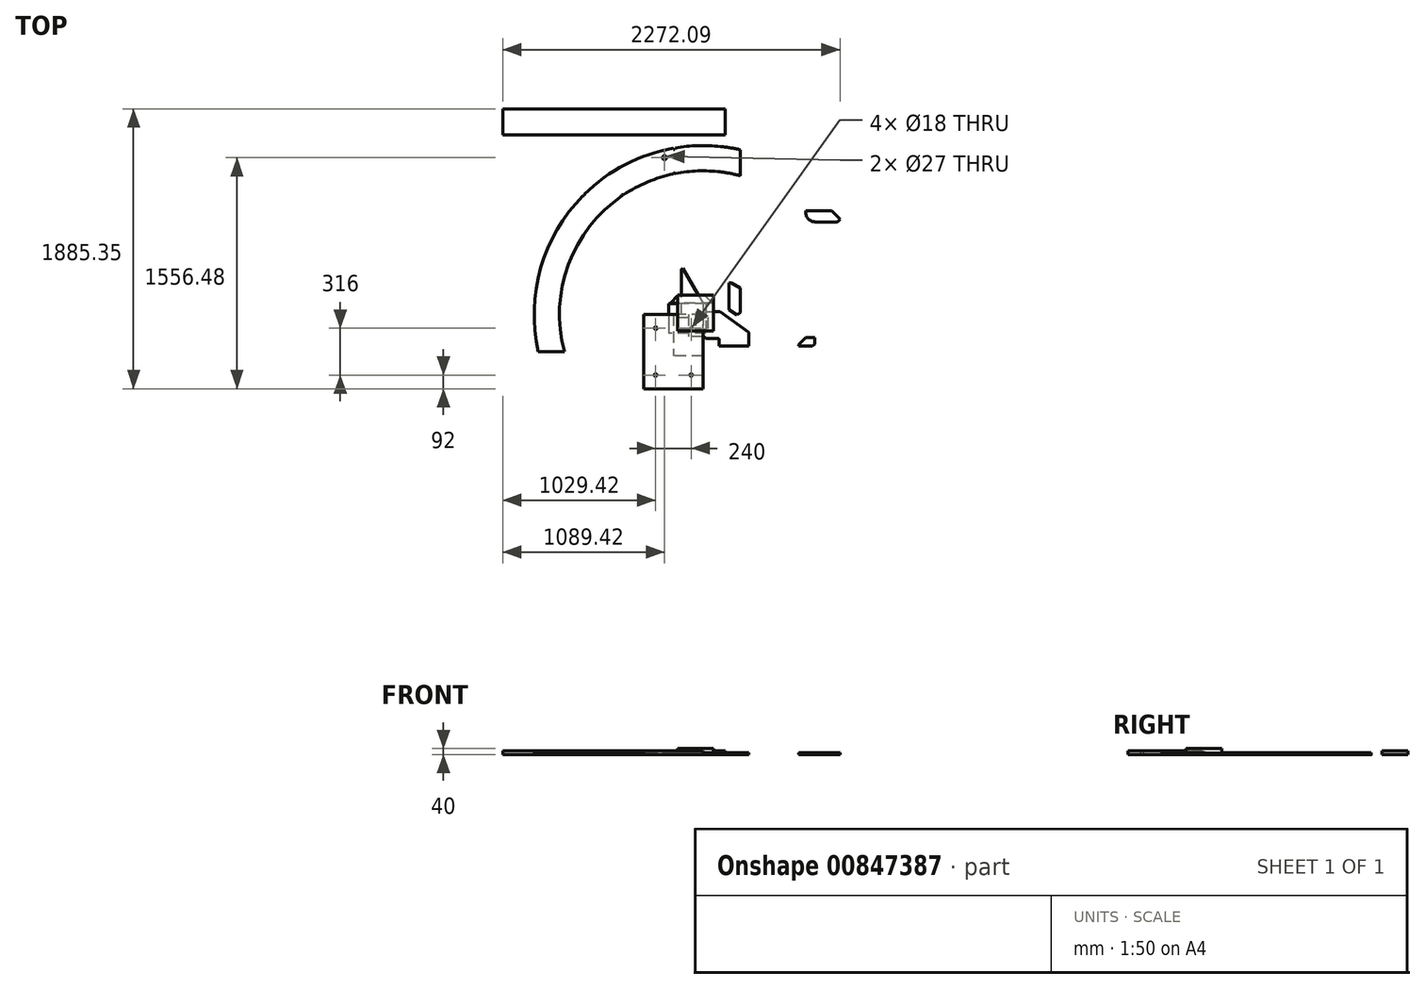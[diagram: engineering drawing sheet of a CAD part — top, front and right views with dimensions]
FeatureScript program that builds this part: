
annotation { "Feature Type Name" : "Feature", "Feature Type Description" : "" }
export const myFeature = defineFeature(function(context is Context, id is Id, definition is map)
    precondition{}
    {
        {
            var Q0;
            Q0=qCreatedBy(makeId("Top.planeOp"),FACE);
            var sketch = newSketch(context, id + "F0", { "sketchPlane" : qUnion([Q0])});
            skArc(sketch, "E0", {"start": v(250.54, 935.02) * mm, "mid": v(186.68, 949.83) * mm, "end": v(121.98, 960.28) * mm});
            skLineSegment(sketch, "E1", {"start": v(250.54, 935.02) * mm, "end": v(250.54, 1110.08) * mm});
            skLineSegment(sketch, "E2", {"start": v(-935.02, -250.54) * mm, "end": v(-1110.08, -250.54) * mm});
            skCircle(sketch, "E3", {"center": v(-260, 1056.48) * mm, "radius": 13.5 * mm});
            skLineSegment(sketch, "E4", {"start": v(-200, 1120.29) * mm, "end": v(-200, 1111.78) * mm});
            skLineSegment(sketch, "E5", {"start": v(116, 1132.07) * mm, "end": v(116, 1126.07) * mm});
            skLineSegment(sketch, "E6", {"start": v(-809.35, 800) * mm, "end": v(-799.3, 800) * mm});
            skLineSegment(sketch, "E7", {"start": v(-799.3, 800) * mm, "end": v(-799.3, 810.04) * mm});
            skLineSegment(sketch, "E8", {"start": v(-200, 1111.78) * mm, "end": v(-191.98, 1111.78) * mm});
            skLineSegment(sketch, "E9", {"start": v(-191.98, 1111.78) * mm, "end": v(-187.26, 1122.49) * mm});
            skLineSegment(sketch, "E10", {"start": v(-200, 954.9) * mm, "end": v(-186.65, 949.83) * mm});
            skLineSegment(sketch, "E11", {"start": v(116, 1126.07) * mm, "end": v(121.39, 1131.5) * mm});
            skLineSegment(sketch, "E12", {"start": v(116, 968.66) * mm, "end": v(121.98, 960.28) * mm});
            skArc(sketch, "E13.trimOffspring", {"start": v(250.54, 1110.08) * mm, "mid": v(186.27, 1122.65) * mm, "end": v(121.39, 1131.5) * mm});
            skPoint(sketch, "E14.start.orphan", {"position": v(0, 1199.9) * mm});
            skLineSegment(sketch, "E15.trimOffspring", {"start": v(-200, 954.9) * mm, "end": v(-200, 947.11) * mm});
            skLineSegment(sketch, "E16.trimOffspring", {"start": v(116, 968.66) * mm, "end": v(116, 961.02) * mm});
            skLineSegment(sketch, "E17.trimOffspring", {"start": v(-550.8, 800) * mm, "end": v(-545, 800) * mm});
            skArc(sketch, "E18.trimOffspring", {"start": v(-809.35, 800) * mm, "mid": v(-1094.06, 313.19) * mm, "end": v(-1110.08, -250.54) * mm});
            skLineSegment(sketch, "E19", {"start": v(-550.8, 800) * mm, "end": v(-550.8, 806.6) * mm});
            skLineSegment(sketch, "E20", {"start": v(-550.8, 806.6) * mm, "end": v(-535.17, 806.6) * mm});
            skArc(sketch, "E21.trimOffspring", {"start": v(-545, 800) * mm, "mid": v(-907.48, 336.9) * mm, "end": v(-935.02, -250.54) * mm});
            skArc(sketch, "E22.trimOffspring", {"start": v(-200, 1120.29) * mm, "mid": v(-523.18, 1010.6) * mm, "end": v(-799.3, 810.04) * mm});
            skArc(sketch, "E23.trimOffspring", {"start": v(-200, 947.11) * mm, "mid": v(-374.24, 892.73) * mm, "end": v(-535.17, 806.6) * mm});
            skArc(sketch, "E24.trimOffspring", {"start": v(116, 961.02) * mm, "mid": v(-35.76, 967.34) * mm, "end": v(-186.65, 949.83) * mm});
            skArc(sketch, "E25.trimOffspring", {"start": v(116, 1132.07) * mm, "mid": v(-35.95, 1137.43) * mm, "end": v(-187.26, 1122.49) * mm});
            skLineSegment(sketch, "E26.bottom", {"start": v(691.59, 699.24) * mm, "end": v(866.59, 699.24) * mm});
            skLineSegment(sketch, "E26.top", {"start": v(756.59, 624.24) * mm, "end": v(866.59, 624.24) * mm});
            skLineSegment(sketch, "E26.left", {"start": v(691.59, 699.24) * mm, "end": v(691.59, 689.24) * mm});
            skLineSegment(sketch, "E26.right", {"start": v(866.59, 699.24) * mm, "end": v(866.59, 624.24) * mm});
            skLineSegment(sketch, "E27", {"start": v(866.59, 699.24) * mm, "end": v(922.67, 643.16) * mm});
            skLineSegment(sketch, "E28", {"start": v(903.76, 624.24) * mm, "end": v(866.59, 624.24) * mm});
            skLineSegment(sketch, "E29", {"start": v(922.67, 643.16) * mm, "end": v(903.76, 624.24) * mm});
            skPoint(sketch, "E30.visualSharp", {"position": v(691.59, 624.24) * mm});
            skArc(sketch, "E30.filletArc", {"start": v(691.59, 689.24) * mm, "mid": v(710.63, 643.28) * mm, "end": v(756.59, 624.24) * mm});
            skPoint(sketch, "E31.orphan", {"position": v(941.59, 624.24) * mm});
            skSolve(sketch);
        }
        {
            var Q0;
            Q0 = qSketchRegion(id + "F0", true);
            extrude(context, id + "F1", {"entities" : qUnion([Q0]), "depth" : 12 * mm, "offsetDistance" : 25 * mm});
        }
        {
            var Q0;
            Q0=qCreatedBy(makeId("Top.planeOp"),FACE);
            var sketch = newSketch(context, id + "F2", { "sketchPlane" : qUnion([Q0])});
            skLineSegment(sketch, "E32.bottom", {"start": v(175.87, 213.2) * mm, "end": v(190.87, 213.2) * mm});
            skLineSegment(sketch, "E32.left", {"start": v(175.87, 213.2) * mm, "end": v(175.87, 33.2) * mm});
            skLineSegment(sketch, "E32.right", {"start": v(250.87, 178.2) * mm, "end": v(250.87, 12.2) * mm});
            skLineSegment(sketch, "E33", {"start": v(190.87, 213.2) * mm, "end": v(250.87, 178.2) * mm});
            skLineSegment(sketch, "E34", {"start": v(175.87, 33.2) * mm, "end": v(227.87, -3.8) * mm});
            skLineSegment(sketch, "E35", {"start": v(227.87, -3.8) * mm, "end": v(250.87, 12.2) * mm});
            skSolve(sketch);
        }
        {
            var Q0;
            Q0 = qSketchRegion(id + "F2", true);
            extrude(context, id + "F3", {"entities" : qUnion([Q0]), "depth" : 10 * mm, "offsetDistance" : 25 * mm});
        }
        {
            var Q0;
            Q0=qCreatedBy(makeId("Top.planeOp"),FACE);
            var sketch = newSketch(context, id + "F4", { "sketchPlane" : qUnion([Q0])});
            skLineSegment(sketch, "E36", {"start": v(-166.74, 130.62) * mm, "end": v(9.26, 130.62) * mm});
            skLineSegment(sketch, "E37", {"start": v(9.26, 130.62) * mm, "end": v(62.3, 77.58) * mm});
            skLineSegment(sketch, "E38", {"start": v(62.3, 77.58) * mm, "end": v(-219.77, 77.58) * mm});
            skLineSegment(sketch, "E39", {"start": v(-219.77, 77.58) * mm, "end": v(-166.74, 130.62) * mm});
            skPoint(sketch, "E40.end.orphan", {"position": v(-166.74, 184.48) * mm});
            skSolve(sketch);
        }
        {
            var Q0;
            Q0 = qSketchRegion(id + "F4", true);
            extrude(context, id + "F5", {"entities" : qUnion([Q0]), "depth" : 10 * mm, "offsetDistance" : 25 * mm});
        }
        {
            var Q0;
            Q0 = qSketchRegion(id + "F0", true);
            extrude(context, id + "F6", {"entities" : qUnion([Q0]), "depth" : 10 * mm, "offsetDistance" : 25 * mm});
        }
        {
            var Q0;
            Q0=qCreatedBy(makeId("Top.planeOp"),FACE);
            var sketch = newSketch(context, id + "F7", { "sketchPlane" : qUnion([Q0])});
            skLineSegment(sketch, "E41.bottom", {"start": v(-1349.42, 1385.35) * mm, "end": v(150.58, 1385.35) * mm});
            skLineSegment(sketch, "E41.top", {"start": v(-1349.42, 1209.35) * mm, "end": v(150.58, 1209.35) * mm});
            skLineSegment(sketch, "E41.left", {"start": v(-1349.42, 1385.35) * mm, "end": v(-1349.42, 1209.35) * mm});
            skLineSegment(sketch, "E41.right", {"start": v(150.58, 1385.35) * mm, "end": v(150.58, 1209.35) * mm});
            skSolve(sketch);
        }
        {
            var Q0;
            Q0 = qSketchRegion(id + "F7", true);
            extrude(context, id + "F8", {"entities" : qUnion([Q0]), "depth" : 12 * mm, "offsetDistance" : 25 * mm});
        }
        {
            var Q0;
            Q0 = qSketchRegion(id + "F7", true);
            extrude(context, id + "F9", {"entities" : qUnion([Q0]), "operationType" : NewBodyOperationType.ADD, "depth" : 25 * mm, "offsetDistance" : 25 * mm});
        }
        {
            var Q0;
            Q0=qCreatedBy(makeId("Top.planeOp"),FACE);
            var sketch = newSketch(context, id + "F10", { "sketchPlane" : qUnion([Q0])});
            skLineSegment(sketch, "E42", {"start": v(750.99, -155) * mm, "end": v(750.99, -198) * mm});
            skLineSegment(sketch, "E43", {"start": v(750.99, -198) * mm, "end": v(735.99, -213) * mm});
            skLineSegment(sketch, "E44", {"start": v(735.99, -213) * mm, "end": v(642.99, -213) * mm});
            skLineSegment(sketch, "E45", {"start": v(642.99, -213) * mm, "end": v(642.99, -203) * mm});
            skLineSegment(sketch, "E46", {"start": v(642.99, -203) * mm, "end": v(692.99, -155) * mm});
            skLineSegment(sketch, "E47", {"start": v(692.99, -155) * mm, "end": v(750.99, -155) * mm});
            skSolve(sketch);
        }
        {
            var Q0;
            Q0 = qSketchRegion(id + "F10", true);
            extrude(context, id + "F11", {"entities" : qUnion([Q0]), "depth" : 12 * mm, "offsetDistance" : 25 * mm});
        }
        {
            var Q0;
            Q0=qCreatedBy(makeId("Top.planeOp"),FACE);
            var sketch = newSketch(context, id + "F12", { "sketchPlane" : qUnion([Q0])});
            skLineSegment(sketch, "E48.bottom", {"start": v(0, 0) * mm, "end": v(-400, 0) * mm});
            skLineSegment(sketch, "E48.top", {"start": v(0, -500) * mm, "end": v(-400, -500) * mm});
            skLineSegment(sketch, "E48.left", {"start": v(0, 0) * mm, "end": v(0, -500) * mm});
            skLineSegment(sketch, "E48.right", {"start": v(-400, 0) * mm, "end": v(-400, -500) * mm});
            skCircle(sketch, "E49", {"center": v(-320, -92) * mm, "radius": 9 * mm});
            skCircle(sketch, "E50", {"center": v(-80, -92) * mm, "radius": 9 * mm});
            skCircle(sketch, "E51", {"center": v(-80, -408) * mm, "radius": 9 * mm});
            skCircle(sketch, "E52", {"center": v(-320, -408) * mm, "radius": 9 * mm});
            skSolve(sketch);
        }
        {
            var Q0;
            Q0 = qSketchRegion(id + "F12", true);
            extrude(context, id + "F13", {"entities" : qUnion([Q0]), "depth" : 16 * mm, "offsetDistance" : 25 * mm});
        }
        {
            var Q0;
            Q0 = qSketchRegion(id + "F12", true);
            extrude(context, id + "F14", {"entities" : qUnion([Q0]), "operationType" : NewBodyOperationType.ADD, "depth" : 25 * mm, "offsetDistance" : 25 * mm});
        }
        {
            var Q0;
            Q0=qCreatedBy(makeId("Top.planeOp"),FACE);
            var sketch = newSketch(context, id + "F15", { "sketchPlane" : qUnion([Q0])});
            skLineSegment(sketch, "E53", {"start": v(0, 0) * mm, "end": v(20, 20) * mm});
            skLineSegment(sketch, "E54", {"start": v(20, 20) * mm, "end": v(113, 20) * mm});
            skLineSegment(sketch, "E55", {"start": v(113, 20) * mm, "end": v(308, -121) * mm});
            skLineSegment(sketch, "E56", {"start": v(308, -121) * mm, "end": v(308, -211) * mm});
            skLineSegment(sketch, "E57", {"start": v(308, -211) * mm, "end": v(108, -211) * mm});
            skLineSegment(sketch, "E58", {"start": v(108, -211) * mm, "end": v(108, -171) * mm});
            skLineSegment(sketch, "E59", {"start": v(98, -161) * mm, "end": v(20, -161) * mm});
            skLineSegment(sketch, "E60", {"start": v(20, -161) * mm, "end": v(0, -141) * mm});
            skLineSegment(sketch, "E61", {"start": v(0, -141) * mm, "end": v(0, 0) * mm});
            skPoint(sketch, "E62.visualSharp", {"position": v(108, -161) * mm});
            skArc(sketch, "E62.filletArc", {"start": v(108, -171) * mm, "mid": v(105.07, -163.93) * mm, "end": v(98, -161) * mm});
            skSolve(sketch);
        }
        {
            var Q0;
            Q0 = qSketchRegion(id + "F15", true);
            extrude(context, id + "F16", {"entities" : qUnion([Q0]), "depth" : 12 * mm, "offsetDistance" : 25 * mm});
        }
        {
            var Q0;
            Q0=qCreatedBy(makeId("Top.planeOp"),FACE);
            var sketch = newSketch(context, id + "F17", { "sketchPlane" : qUnion([Q0])});
            skLineSegment(sketch, "E63.bottom", {"start": v(0, 0) * mm, "end": v(-100, 0) * mm});
            skLineSegment(sketch, "E63.top", {"start": v(0, -150) * mm, "end": v(-100, -150) * mm});
            skLineSegment(sketch, "E63.left", {"start": v(0, 0) * mm, "end": v(0, -150) * mm});
            skLineSegment(sketch, "E63.right", {"start": v(-100, 0) * mm, "end": v(-100, -150) * mm});
            skSolve(sketch);
        }
        {
            var Q0;
            Q0 = qSketchRegion(id + "F17", true);
            extrude(context, id + "F18", {"entities" : qUnion([Q0]), "depth" : 8 * mm, "offsetDistance" : 25 * mm});
        }
        {
            var Q0;
            Q0=qCreatedBy(makeId("Top.planeOp"),FACE);
            var sketch = newSketch(context, id + "F19", { "sketchPlane" : qUnion([Q0])});
            skLineSegment(sketch, "E64.bottom", {"start": v(0, 0) * mm, "end": v(-50, 0) * mm});
            skLineSegment(sketch, "E64.top", {"start": v(0, -100) * mm, "end": v(-50, -100) * mm});
            skLineSegment(sketch, "E64.left", {"start": v(0, 0) * mm, "end": v(0, -100) * mm});
            skLineSegment(sketch, "E64.right", {"start": v(-50, 0) * mm, "end": v(-50, -100) * mm});
            skSolve(sketch);
        }
        {
            var Q0;
            Q0 = qSketchRegion(id + "F19", true);
            extrude(context, id + "F20", {"entities" : qUnion([Q0]), "depth" : 12 * mm, "offsetDistance" : 25 * mm});
        }
        {
            var Q0;
            Q0=qCreatedBy(makeId("Top.planeOp"),FACE);
            var sketch = newSketch(context, id + "F21", { "sketchPlane" : qUnion([Q0])});
            skLineSegment(sketch, "E65.bottom", {"start": v(-48.65, 15.25) * mm, "end": v(1.35, 15.25) * mm});
            skLineSegment(sketch, "E65.top", {"start": v(-48.65, -34.75) * mm, "end": v(1.35, -34.75) * mm});
            skLineSegment(sketch, "E65.left", {"start": v(-48.65, 15.25) * mm, "end": v(-48.65, -34.75) * mm});
            skLineSegment(sketch, "E65.right", {"start": v(1.35, 15.25) * mm, "end": v(1.35, -34.75) * mm});
            skSolve(sketch);
        }
        {
            var Q0;
            Q0 = qSketchRegion(id + "F21", true);
            extrude(context, id + "F22", {"entities" : qUnion([Q0]), "depth" : 12 * mm, "offsetDistance" : 25 * mm});
        }
        {
            var Q0;
            Q0=qCreatedBy(makeId("Top.planeOp"),FACE);
            var sketch = newSketch(context, id + "F23", { "sketchPlane" : qUnion([Q0])});
            skLineSegment(sketch, "E66.bottom", {"start": v(68.98, 130.4) * mm, "end": v(-171.02, 130.4) * mm});
            skLineSegment(sketch, "E66.top", {"start": v(68.98, -109.6) * mm, "end": v(-171.02, -109.6) * mm});
            skLineSegment(sketch, "E66.left", {"start": v(68.98, 130.4) * mm, "end": v(68.98, -109.6) * mm});
            skLineSegment(sketch, "E66.right", {"start": v(-171.02, 130.4) * mm, "end": v(-171.02, -109.6) * mm});
            skSolve(sketch);
        }
        {
            var Q0;
            Q0 = qSketchRegion(id + "F23", true);
            extrude(context, id + "F24", {"entities" : qUnion([Q0]), "depth" : 40 * mm, "offsetDistance" : 25 * mm});
        }
        {
            var Q0;
            Q0=qCreatedBy(makeId("Top.planeOp"),FACE);
            var sketch = newSketch(context, id + "F25", { "sketchPlane" : qUnion([Q0])});
            skLineSegment(sketch, "E67", {"start": v(0, 0) * mm, "end": v(-145, 0) * mm});
            skLineSegment(sketch, "E68", {"start": v(-145, 0) * mm, "end": v(-145, 306) * mm});
            skLineSegment(sketch, "E69", {"start": v(-145, 306) * mm, "end": v(-135, 312) * mm});
            skLineSegment(sketch, "E70", {"start": v(-135, 312) * mm, "end": v(0, 78) * mm});
            skLineSegment(sketch, "E71", {"start": v(0, 78) * mm, "end": v(0, 0) * mm});
            skSolve(sketch);
        }
        {
            var Q0;
            Q0 = qSketchRegion(id + "F25", true);
            extrude(context, id + "F26", {"entities" : qUnion([Q0]), "depth" : 10 * mm, "offsetDistance" : 25 * mm});
        }
        {
            var Q0;
            Q0=qCreatedBy(makeId("Top.planeOp"),FACE);
            var sketch = newSketch(context, id + "F27", { "sketchPlane" : qUnion([Q0])});
            skLineSegment(sketch, "E72.bottom", {"start": v(0, 0) * mm, "end": v(-200, 0) * mm});
            skLineSegment(sketch, "E72.top", {"start": v(0, -280) * mm, "end": v(-200, -280) * mm});
            skLineSegment(sketch, "E72.left", {"start": v(0, 0) * mm, "end": v(0, -280) * mm});
            skLineSegment(sketch, "E72.right", {"start": v(-200, 0) * mm, "end": v(-200, -280) * mm});
            skSolve(sketch);
        }
        {
            var Q0;
            Q0 = qSketchRegion(id + "F27", true);
            extrude(context, id + "F28", {"entities" : qUnion([Q0]), "depth" : 10 * mm, "offsetDistance" : 25 * mm});
        }
        {
            var Q0;
            Q0=qCreatedBy(makeId("Top.planeOp"),FACE);
            var sketch = newSketch(context, id + "F29", { "sketchPlane" : qUnion([Q0])});
            skLineSegment(sketch, "E73.bottom", {"start": v(-167.6, -19.05) * mm, "end": v(32.4, -19.05) * mm});
            skLineSegment(sketch, "E73.top", {"start": v(-167.6, -97.05) * mm, "end": v(32.4, -97.05) * mm});
            skLineSegment(sketch, "E73.left", {"start": v(-167.6, -19.05) * mm, "end": v(-167.6, -97.05) * mm});
            skLineSegment(sketch, "E73.right", {"start": v(32.4, -19.05) * mm, "end": v(32.4, -97.05) * mm});
            skSolve(sketch);
        }
        {
            var Q0;
            Q0 = qSketchRegion(id + "F29", true);
            extrude(context, id + "F30", {"entities" : qUnion([Q0]), "depth" : 10 * mm, "offsetDistance" : 25 * mm});
        }
        {
            var Q0;
            Q0=qCreatedBy(makeId("Top.planeOp"),FACE);
            var sketch = newSketch(context, id + "F31", { "sketchPlane" : qUnion([Q0])});
            skLineSegment(sketch, "E74.bottom", {"start": v(19.62, 73.83) * mm, "end": v(-230.38, 73.83) * mm});
            skLineSegment(sketch, "E74.top", {"start": v(19.62, -126.17) * mm, "end": v(-230.38, -126.17) * mm});
            skLineSegment(sketch, "E74.left", {"start": v(19.62, 73.83) * mm, "end": v(19.62, -126.17) * mm});
            skLineSegment(sketch, "E74.right", {"start": v(-230.38, 73.83) * mm, "end": v(-230.38, -126.17) * mm});
            skSolve(sketch);
        }
        {
            var Q0;
            Q0 = qSketchRegion(id + "F31", true);
            extrude(context, id + "F32", {"entities" : qUnion([Q0]), "depth" : 10 * mm, "offsetDistance" : 25 * mm});
        }
    });
